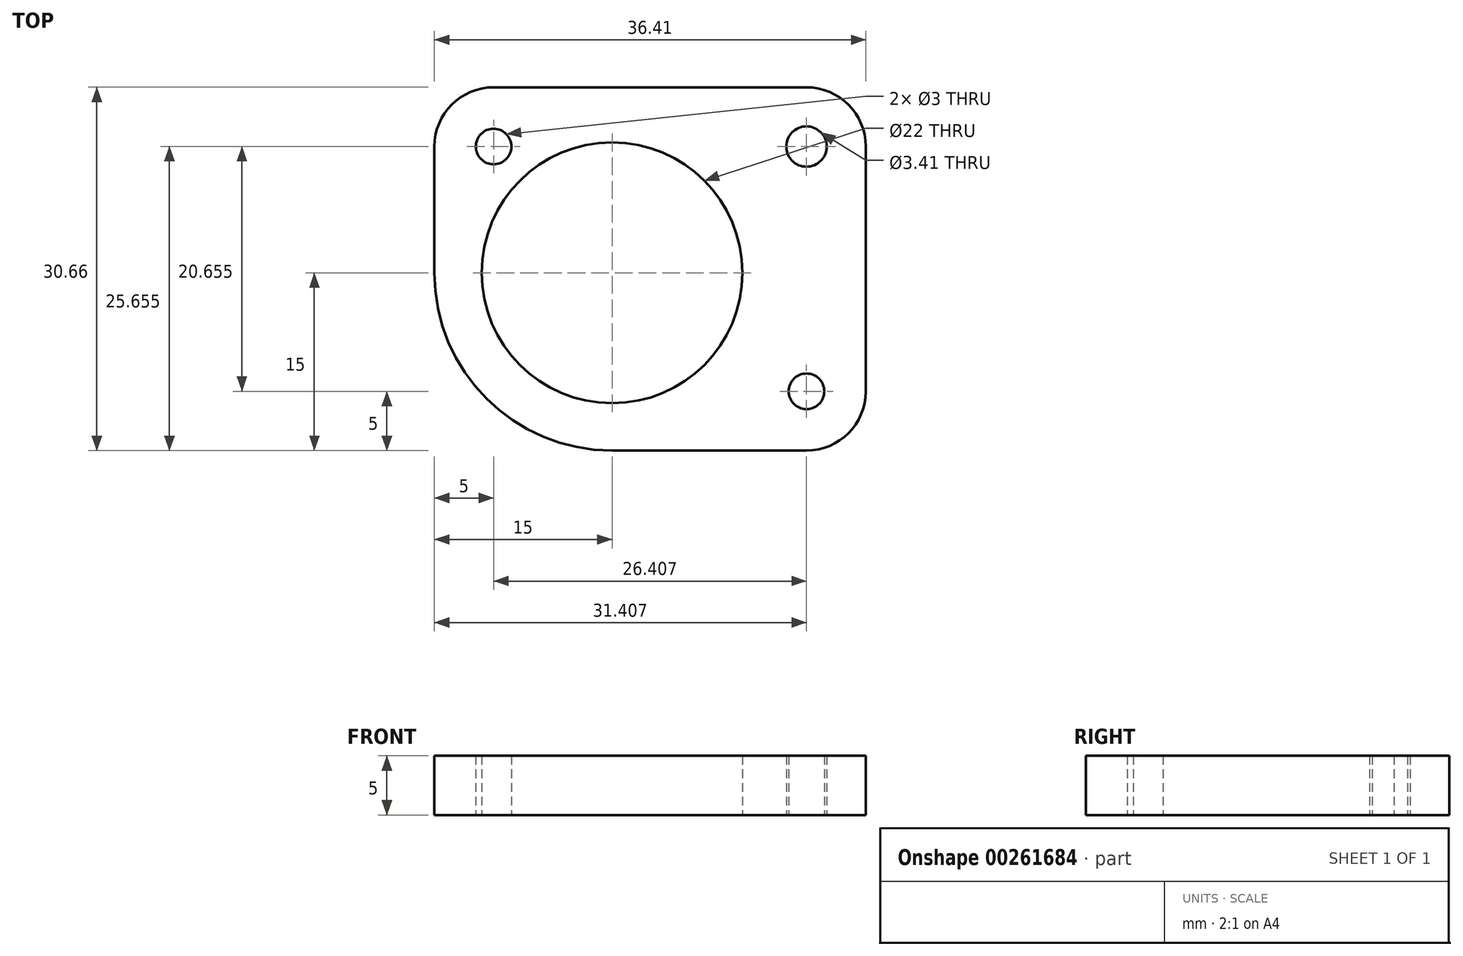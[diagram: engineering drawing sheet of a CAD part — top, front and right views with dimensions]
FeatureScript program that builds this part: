
annotation { "Feature Type Name" : "Feature", "Feature Type Description" : "" }
export const myFeature = defineFeature(function(context is Context, id is Id, definition is map)
    precondition{}
    {
        {
            var Q0;
            Q0=qCreatedBy(makeId("Top.planeOp"),FACE);
            var sketch = newSketch(context, id + "F0", { "sketchPlane" : qUnion([Q0])});
            skCircle(sketch, "E0", {"center": v(0, 0) * mm, "radius": 11 * mm});
            skLineSegment(sketch, "E1.bottom", {"start": v(16.4, -15) * mm, "end": v(0, -15) * mm});
            skLineSegment(sketch, "E1.top", {"start": v(16.4, 15.66) * mm, "end": v(-10, 15.66) * mm});
            skLineSegment(sketch, "E1.left", {"start": v(21.4, -10) * mm, "end": v(21.4, 10.66) * mm});
            skLineSegment(sketch, "E1.right", {"start": v(-15, 0) * mm, "end": v(-15, 10.66) * mm});
            skPoint(sketch, "E2.visualSharp", {"position": v(-15, -15) * mm});
            skArc(sketch, "E2.filletArc", {"start": v(-15, 0) * mm, "mid": v(-10.6, -10.6) * mm, "end": v(0, -15) * mm});
            skCircle(sketch, "E3", {"center": v(16.4, -10) * mm, "radius": 1.5 * mm});
            skCircle(sketch, "E4", {"center": v(16.4, 10.66) * mm, "radius": 1.7 * mm});
            skCircle(sketch, "E5", {"center": v(-10, 10.66) * mm, "radius": 1.5 * mm});
            skPoint(sketch, "E6.visualSharp", {"position": v(21.4, -15) * mm});
            skArc(sketch, "E6.filletArc", {"start": v(16.4, -15) * mm, "mid": v(19.94, -13.54) * mm, "end": v(21.4, -10) * mm});
            skPoint(sketch, "E7.visualSharp", {"position": v(21.4, 15.66) * mm});
            skArc(sketch, "E7.filletArc", {"start": v(21.4, 10.66) * mm, "mid": v(19.94, 14.2) * mm, "end": v(16.4, 15.66) * mm});
            skPoint(sketch, "E8.visualSharp", {"position": v(-15, 15.66) * mm});
            skArc(sketch, "E8.filletArc", {"start": v(-10, 15.66) * mm, "mid": v(-13.54, 14.2) * mm, "end": v(-15, 10.66) * mm});
            skSolve(sketch);
        }
        {
            var Q0;
            Q0=makeQuery(id+"F0.imprint","IMPRINT",FACE,{"disambiguationData":[TD([[makeQuery(id+"F0.imprint","IMPRINT",EDGE,{"derivedFrom":sQuery(id+"F0.wireOp",EDGE,"E0")}),-1.0]])]});
            extrude(context, id + "F1", {"entities" : qUnion([Q0]), "depth" : 5 * mm});
        }
    });
